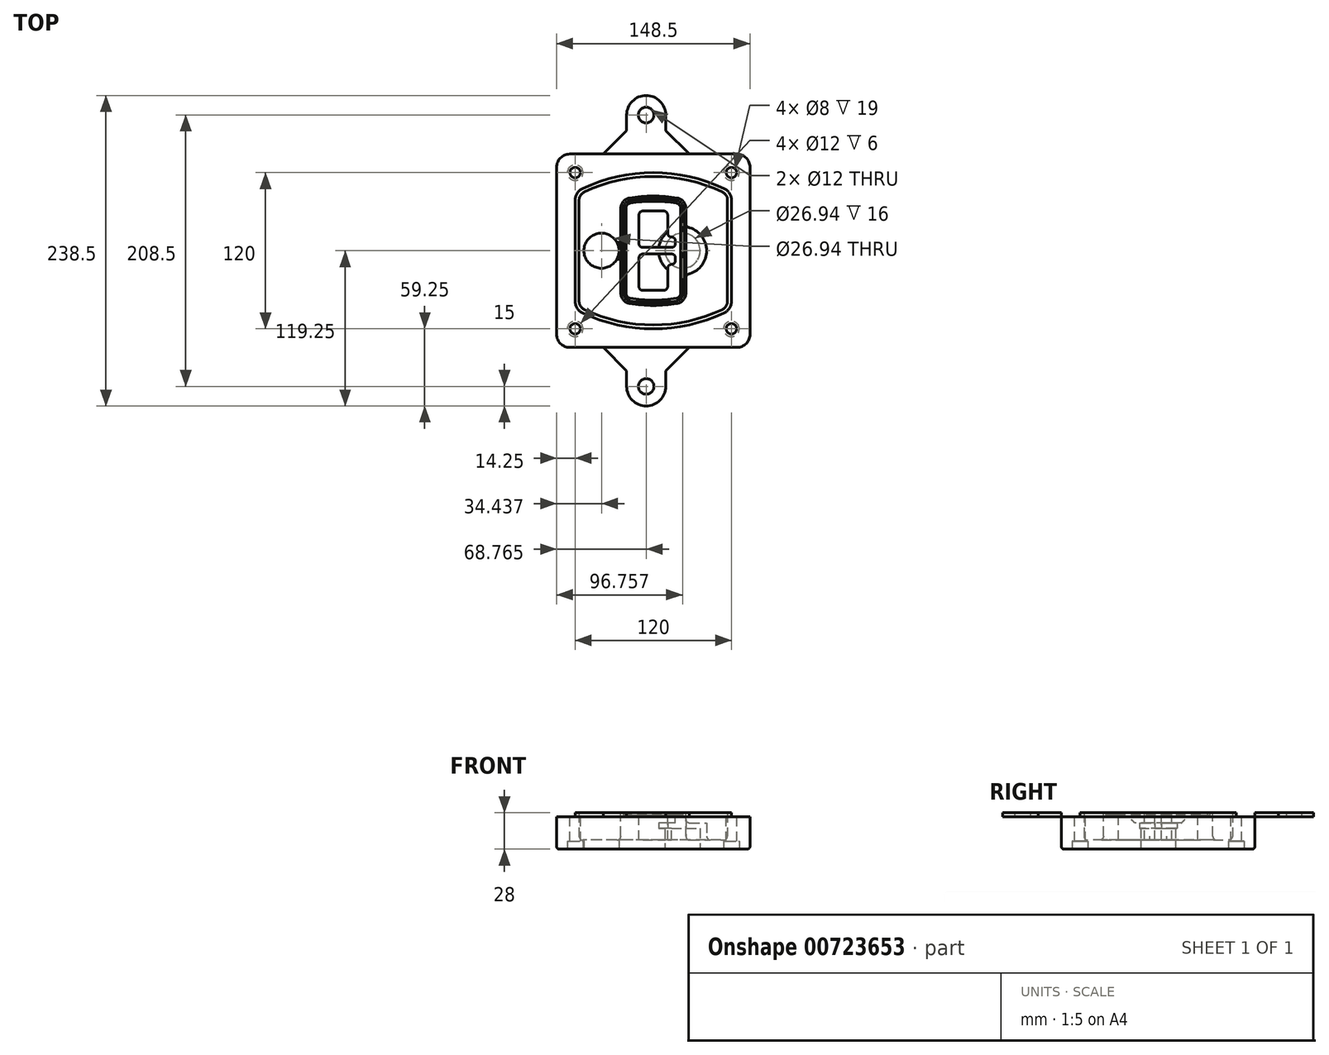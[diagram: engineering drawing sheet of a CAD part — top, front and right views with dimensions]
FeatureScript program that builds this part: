
annotation { "Feature Type Name" : "Feature", "Feature Type Description" : "" }
export const myFeature = defineFeature(function(context is Context, id is Id, definition is map)
    precondition{}
    {
        {
            var Q0;
            Q0=qCreatedBy(makeId("Top.planeOp"),FACE);
            var sketch = newSketch(context, id + "F0", { "sketchPlane" : qUnion([Q0])});
            skPoint(sketch, "E0.rect.middle", {"position": v(0, 0) * mm});
            skLineSegment(sketch, "E1.bottom", {"start": v(-64.25, -74.25) * mm, "end": v(64.25, -74.25) * mm});
            skLineSegment(sketch, "E1.top", {"start": v(-64.25, 74.25) * mm, "end": v(64.25, 74.25) * mm});
            skLineSegment(sketch, "E1.left", {"start": v(-74.25, -64.25) * mm, "end": v(-74.25, 64.25) * mm});
            skLineSegment(sketch, "E1.right", {"start": v(74.25, -64.25) * mm, "end": v(74.25, 64.25) * mm});
            skLineSegment(sketch, "E2", {"start": v(-74.25, 74.25) * mm, "end": v(74.25, -74.25) * mm, "construction": true});
            skLineSegment(sketch, "E3", {"start": v(74.25, 74.25) * mm, "end": v(-74.25, -74.25) * mm, "construction": true});
            skCircle(sketch, "E4", {"center": v(-60, 60) * mm, "radius": 4 * mm});
            skCircle(sketch, "E5", {"center": v(60, 60) * mm, "radius": 4 * mm});
            skCircle(sketch, "E6", {"center": v(60, -60) * mm, "radius": 4 * mm});
            skCircle(sketch, "E7", {"center": v(-60, -60) * mm, "radius": 4 * mm});
            skLineSegment(sketch, "E8", {"start": v(-60, 60) * mm, "end": v(60, 60) * mm, "construction": true});
            skLineSegment(sketch, "E9", {"start": v(60, 60) * mm, "end": v(60, -60) * mm, "construction": true});
            skLineSegment(sketch, "E10", {"start": v(60, -60) * mm, "end": v(-60, -60) * mm, "construction": true});
            skLineSegment(sketch, "E11", {"start": v(-60, -60) * mm, "end": v(-60, 60) * mm, "construction": true});
            skLineSegment(sketch, "E12", {"start": v(-60, 38.83) * mm, "end": v(-60, -38.83) * mm});
            skLineSegment(sketch, "E13", {"start": v(60, 38.83) * mm, "end": v(60, -38.83) * mm});
            skArc(sketch, "E14", {"start": v(54.26, 47.88) * mm, "mid": v(0, 60) * mm, "end": v(-54.26, 47.88) * mm});
            skArc(sketch, "E15", {"start": v(-54.26, -47.88) * mm, "mid": v(0, -60) * mm, "end": v(54.26, -47.88) * mm});
            skLineSegment(sketch, "E16", {"start": v(-60, 0) * mm, "end": v(60, 0) * mm, "construction": true});
            skPoint(sketch, "E17.visualSharp", {"position": v(-60, -45) * mm});
            skArc(sketch, "E17.filletArc", {"start": v(-60, -38.83) * mm, "mid": v(-58.44, -44.2) * mm, "end": v(-54.26, -47.88) * mm});
            skPoint(sketch, "E18.visualSharp", {"position": v(-60, 45) * mm});
            skArc(sketch, "E18.filletArc", {"start": v(-54.26, 47.88) * mm, "mid": v(-58.44, 44.2) * mm, "end": v(-60, 38.83) * mm});
            skPoint(sketch, "E19.visualSharp", {"position": v(60, 45) * mm});
            skArc(sketch, "E19.filletArc", {"start": v(60, 38.83) * mm, "mid": v(58.44, 44.2) * mm, "end": v(54.26, 47.88) * mm});
            skPoint(sketch, "E20.visualSharp", {"position": v(60, -45) * mm});
            skArc(sketch, "E20.filletArc", {"start": v(54.26, -47.88) * mm, "mid": v(58.44, -44.2) * mm, "end": v(60, -38.83) * mm});
            skPoint(sketch, "E21.visualSharp", {"position": v(-74.25, 74.25) * mm});
            skArc(sketch, "E21.filletArc", {"start": v(-64.25, 74.25) * mm, "mid": v(-71.32, 71.32) * mm, "end": v(-74.25, 64.25) * mm});
            skPoint(sketch, "E22.visualSharp", {"position": v(74.25, 74.25) * mm});
            skArc(sketch, "E22.filletArc", {"start": v(74.25, 64.25) * mm, "mid": v(71.32, 71.32) * mm, "end": v(64.25, 74.25) * mm});
            skPoint(sketch, "E23.visualSharp", {"position": v(74.25, -74.25) * mm});
            skArc(sketch, "E23.filletArc", {"start": v(64.25, -74.25) * mm, "mid": v(71.32, -71.32) * mm, "end": v(74.25, -64.25) * mm});
            skPoint(sketch, "E24.visualSharp", {"position": v(-74.25, -74.25) * mm});
            skArc(sketch, "E24.filletArc", {"start": v(-74.25, -64.25) * mm, "mid": v(-71.32, -71.32) * mm, "end": v(-64.25, -74.25) * mm});
            skArc(sketch, "E25.0", {"start": v(57, 38.83) * mm, "mid": v(55.9, 42.58) * mm, "end": v(52.98, 45.17) * mm});
            skLineSegment(sketch, "E25.1", {"start": v(57, 38.83) * mm, "end": v(57, -38.83) * mm});
            skArc(sketch, "E25.2", {"start": v(52.98, -45.17) * mm, "mid": v(55.9, -42.58) * mm, "end": v(57, -38.83) * mm});
            skArc(sketch, "E25.3", {"start": v(-52.98, -45.17) * mm, "mid": v(0, -57) * mm, "end": v(52.98, -45.17) * mm});
            skArc(sketch, "E25.4", {"start": v(-57, -38.83) * mm, "mid": v(-55.9, -42.58) * mm, "end": v(-52.98, -45.17) * mm});
            skArc(sketch, "E25.5", {"start": v(52.98, 45.17) * mm, "mid": v(0, 57) * mm, "end": v(-52.98, 45.17) * mm});
            skLineSegment(sketch, "E25.6", {"start": v(-57, 38.83) * mm, "end": v(-57, -38.83) * mm});
            skArc(sketch, "E25.7", {"start": v(-52.98, 45.17) * mm, "mid": v(-55.9, 42.58) * mm, "end": v(-57, 38.83) * mm});
            skArc(sketch, "E26.0", {"start": v(-55.96, 51.5) * mm, "mid": v(-61.82, 46.33) * mm, "end": v(-64, 38.83) * mm});
            skArc(sketch, "E26.1", {"start": v(55.96, 51.5) * mm, "mid": v(0, 64) * mm, "end": v(-55.96, 51.5) * mm});
            skArc(sketch, "E26.2", {"start": v(64, 38.83) * mm, "mid": v(61.82, 46.33) * mm, "end": v(55.96, 51.5) * mm});
            skLineSegment(sketch, "E26.3", {"start": v(64, 38.83) * mm, "end": v(64, -38.83) * mm});
            skArc(sketch, "E26.4", {"start": v(55.96, -51.5) * mm, "mid": v(61.82, -46.33) * mm, "end": v(64, -38.83) * mm});
            skLineSegment(sketch, "E26.5", {"start": v(-64, 38.83) * mm, "end": v(-64, -38.83) * mm});
            skArc(sketch, "E26.6", {"start": v(-55.96, -51.5) * mm, "mid": v(0, -64) * mm, "end": v(55.96, -51.5) * mm});
            skArc(sketch, "E26.7", {"start": v(-64, -38.83) * mm, "mid": v(-61.82, -46.33) * mm, "end": v(-55.96, -51.5) * mm});
            skSolve(sketch);
        }
        {
            var Q0;
            Q0=makeQuery(id+"F0.imprint","IMPRINT",FACE,{"disambiguationData":[TD([[makeQuery(id+"F0.imprint","IMPRINT",EDGE,{"derivedFrom":sQuery(id+"F0.wireOp",EDGE,"E1.bottom")}),1.0]])]});
            var Q1;
            Q1=makeQuery(id+"F0.imprint","IMPRINT",FACE,{"disambiguationData":[TD([[makeQuery(id+"F0.imprint","IMPRINT",EDGE,{"derivedFrom":sQuery(id+"F0.wireOp",EDGE,"E12")}),1.0]])]});
            var Q2;
            Q2=makeQuery(id+"F0.imprint","IMPRINT",FACE,{"disambiguationData":[TD([[makeQuery(id+"F0.imprint","IMPRINT",EDGE,{"derivedFrom":sQuery(id+"F0.wireOp",EDGE,"E25.0")}),1.0]])]});
            var Q3;
            Q3=makeQuery(id+"F0.imprint","IMPRINT",FACE,{"disambiguationData":[TD([[makeQuery(id+"F0.imprint","IMPRINT",EDGE,{"derivedFrom":sQuery(id+"F0.wireOp",EDGE,"E12")}),-1.0]])]});
            extrude(context, id + "F1", {"entities" : qUnion([Q0, Q1, Q2, Q3]), "oppositeDirection" : true, "depth" : 25 * mm});
        }
        {
            var Q0;
            Q0=makeQuery(id+"F0.imprint","IMPRINT",FACE,{"disambiguationData":[TD([[makeQuery(id+"F0.imprint","IMPRINT",EDGE,{"derivedFrom":sQuery(id+"F0.wireOp",EDGE,"E12")}),1.0]])]});
            extrude(context, id + "F2", {"entities" : qUnion([Q0]), "operationType" : NewBodyOperationType.ADD, "depth" : 3 * mm, "offsetDistance" : 25 * mm});
        }
        {
            var Q0;
            Q0=makeQuery(id+"F0.imprint","IMPRINT",FACE,{"disambiguationData":[TD([[makeQuery(id+"F0.imprint","IMPRINT",EDGE,{"derivedFrom":sQuery(id+"F0.wireOp",EDGE,"E25.0")}),1.0]])]});
            extrude(context, id + "F3", {"entities" : qUnion([Q0]), "operationType" : NewBodyOperationType.REMOVE, "oppositeDirection" : true, "depth" : 18 * mm});
        }
        {
            var Q0;
            Q0=makeQuery(id+"F2.opExtrude","CAP_FACE",FACE,{"disambiguationData":[OSD([sQuery(id+"F0.wireOp",EDGE,"E12"),sQuery(id+"F0.wireOp",EDGE,"E13"),sQuery(id+"F0.wireOp",EDGE,"E14"),sQuery(id+"F0.wireOp",EDGE,"E15"),sQuery(id+"F0.wireOp",EDGE,"E17.filletArc"),sQuery(id+"F0.wireOp",EDGE,"E18.filletArc"),sQuery(id+"F0.wireOp",EDGE,"E19.filletArc"),sQuery(id+"F0.wireOp",EDGE,"E20.filletArc"),sQuery(id+"F0.wireOp",EDGE,"E25.0"),sQuery(id+"F0.wireOp",EDGE,"E25.1"),sQuery(id+"F0.wireOp",EDGE,"E25.2"),sQuery(id+"F0.wireOp",EDGE,"E25.3"),sQuery(id+"F0.wireOp",EDGE,"E25.4"),sQuery(id+"F0.wireOp",EDGE,"E25.5"),sQuery(id+"F0.wireOp",EDGE,"E25.6"),sQuery(id+"F0.wireOp",EDGE,"E25.7")])],"isStart":false});
            var sketch = newSketch(context, id + "F4", { "sketchPlane" : qUnion([Q0])});
            skArc(sketch, "E27.0", {"start": v(-18.34, -40.45) * mm, "mid": v(0, -42) * mm, "end": v(18.34, -40.45) * mm});
            skArc(sketch, "E28.0", {"start": v(18.34, 40.45) * mm, "mid": v(0, 42) * mm, "end": v(-18.34, 40.45) * mm});
            skLineSegment(sketch, "E29", {"start": v(-25, 32.57) * mm, "end": v(-25, -32.57) * mm});
            skLineSegment(sketch, "E30", {"start": v(25, 32.57) * mm, "end": v(25, -32.57) * mm});
            skLineSegment(sketch, "E31", {"start": v(-25, 39.1) * mm, "end": v(25, 39.1) * mm, "construction": true});
            skLineSegment(sketch, "E32", {"start": v(-25, -39.1) * mm, "end": v(25, -39.1) * mm, "construction": true});
            skPoint(sketch, "E33.visualSharp", {"position": v(-25, 39.1) * mm});
            skArc(sketch, "E33.filletArc", {"start": v(-18.34, 40.45) * mm, "mid": v(-23.11, 37.73) * mm, "end": v(-25, 32.57) * mm});
            skPoint(sketch, "E34.visualSharp", {"position": v(25, 39.1) * mm});
            skArc(sketch, "E34.filletArc", {"start": v(25, 32.57) * mm, "mid": v(23.11, 37.73) * mm, "end": v(18.34, 40.45) * mm});
            skPoint(sketch, "E35.visualSharp", {"position": v(25, -39.1) * mm});
            skArc(sketch, "E35.filletArc", {"start": v(18.34, -40.45) * mm, "mid": v(23.11, -37.73) * mm, "end": v(25, -32.57) * mm});
            skPoint(sketch, "E36.visualSharp", {"position": v(-25, -39.1) * mm});
            skArc(sketch, "E36.filletArc", {"start": v(-25, -32.57) * mm, "mid": v(-23.11, -37.73) * mm, "end": v(-18.34, -40.45) * mm});
            skArc(sketch, "E37.0", {"start": v(52.98, 45.17) * mm, "mid": v(0, 57) * mm, "end": v(-52.98, 45.17) * mm});
            skArc(sketch, "E37.1", {"start": v(-52.98, 45.17) * mm, "mid": v(-55.9, 42.58) * mm, "end": v(-57, 38.83) * mm});
            skLineSegment(sketch, "E37.2", {"start": v(-57, 38.83) * mm, "end": v(-57, -38.83) * mm});
            skArc(sketch, "E37.3", {"start": v(-57, -38.83) * mm, "mid": v(-55.9, -42.58) * mm, "end": v(-52.98, -45.17) * mm});
            skArc(sketch, "E37.4", {"start": v(-52.98, -45.17) * mm, "mid": v(0, -57) * mm, "end": v(52.98, -45.17) * mm});
            skArc(sketch, "E37.5", {"start": v(52.98, -45.17) * mm, "mid": v(55.9, -42.58) * mm, "end": v(57, -38.83) * mm});
            skLineSegment(sketch, "E37.6", {"start": v(57, 38.83) * mm, "end": v(57, -38.83) * mm});
            skArc(sketch, "E37.7", {"start": v(57, 38.83) * mm, "mid": v(55.9, 42.58) * mm, "end": v(52.98, 45.17) * mm});
            skLineSegment(sketch, "E38.0", {"start": v(23, 32.57) * mm, "end": v(23, -32.57) * mm});
            skArc(sketch, "E38.1", {"start": v(18, -38.48) * mm, "mid": v(21.58, -36.44) * mm, "end": v(23, -32.57) * mm});
            skArc(sketch, "E38.2", {"start": v(-18, -38.48) * mm, "mid": v(0, -40) * mm, "end": v(18, -38.48) * mm});
            skArc(sketch, "E38.3", {"start": v(-23, -32.57) * mm, "mid": v(-21.58, -36.44) * mm, "end": v(-18, -38.48) * mm});
            skLineSegment(sketch, "E38.4", {"start": v(-23, 32.57) * mm, "end": v(-23, -32.57) * mm});
            skArc(sketch, "E38.5", {"start": v(23, 32.57) * mm, "mid": v(21.58, 36.44) * mm, "end": v(18, 38.48) * mm});
            skArc(sketch, "E38.6", {"start": v(-18, 38.48) * mm, "mid": v(-21.58, 36.44) * mm, "end": v(-23, 32.57) * mm});
            skArc(sketch, "E38.7", {"start": v(18, 38.48) * mm, "mid": v(0, 40) * mm, "end": v(-18, 38.48) * mm});
            skArc(sketch, "E39.0", {"start": v(21, 32.57) * mm, "mid": v(20.06, 35.15) * mm, "end": v(17.67, 36.5) * mm});
            skLineSegment(sketch, "E39.1", {"start": v(21, 32.57) * mm, "end": v(21, -32.57) * mm});
            skArc(sketch, "E39.2", {"start": v(17.67, -36.5) * mm, "mid": v(20.06, -35.15) * mm, "end": v(21, -32.57) * mm});
            skArc(sketch, "E39.3", {"start": v(-17.67, -36.5) * mm, "mid": v(0, -38) * mm, "end": v(17.67, -36.5) * mm});
            skArc(sketch, "E39.4", {"start": v(-21, -32.57) * mm, "mid": v(-20.06, -35.15) * mm, "end": v(-17.67, -36.5) * mm});
            skArc(sketch, "E39.5", {"start": v(17.67, 36.5) * mm, "mid": v(0, 38) * mm, "end": v(-17.67, 36.5) * mm});
            skLineSegment(sketch, "E39.6", {"start": v(-21, 32.57) * mm, "end": v(-21, -32.57) * mm});
            skArc(sketch, "E39.7", {"start": v(-17.67, 36.5) * mm, "mid": v(-20.06, 35.15) * mm, "end": v(-21, 32.57) * mm});
            skLineSegment(sketch, "E40", {"start": v(-25, 0) * mm, "end": v(25, 0) * mm, "construction": true});
            skLineSegment(sketch, "E41", {"start": v(-11, 5.5) * mm, "end": v(-11, 27.5) * mm});
            skLineSegment(sketch, "E42", {"start": v(-8, 30.5) * mm, "end": v(8, 30.5) * mm});
            skLineSegment(sketch, "E43", {"start": v(11, 27.5) * mm, "end": v(11, 13.5) * mm});
            skLineSegment(sketch, "E44", {"start": v(14, 10.5) * mm, "end": v(14, 10.5) * mm});
            skLineSegment(sketch, "E45", {"start": v(17, 7.5) * mm, "end": v(17, 5.5) * mm});
            skLineSegment(sketch, "E46", {"start": v(14, 2.5) * mm, "end": v(-8, 2.5) * mm});
            skPoint(sketch, "E47.visualSharp", {"position": v(-11, 30.5) * mm});
            skArc(sketch, "E47.filletArc", {"start": v(-8, 30.5) * mm, "mid": v(-10.12, 29.62) * mm, "end": v(-11, 27.5) * mm});
            skPoint(sketch, "E48.visualSharp", {"position": v(11, 30.5) * mm});
            skArc(sketch, "E48.filletArc", {"start": v(11, 27.5) * mm, "mid": v(10.12, 29.62) * mm, "end": v(8, 30.5) * mm});
            skPoint(sketch, "E49.visualSharp", {"position": v(11, 10.5) * mm});
            skArc(sketch, "E49.filletArc", {"start": v(11, 13.5) * mm, "mid": v(11.88, 11.38) * mm, "end": v(14, 10.5) * mm});
            skPoint(sketch, "E50.visualSharp", {"position": v(17, 10.5) * mm});
            skArc(sketch, "E50.filletArc", {"start": v(17, 7.5) * mm, "mid": v(16.12, 9.62) * mm, "end": v(14, 10.5) * mm});
            skPoint(sketch, "E51.visualSharp", {"position": v(17, 2.5) * mm});
            skArc(sketch, "E51.filletArc", {"start": v(14, 2.5) * mm, "mid": v(16.12, 3.38) * mm, "end": v(17, 5.5) * mm});
            skPoint(sketch, "E52.visualSharp", {"position": v(-11, 2.5) * mm});
            skArc(sketch, "E52.filletArc", {"start": v(-11, 5.5) * mm, "mid": v(-10.12, 3.38) * mm, "end": v(-8, 2.5) * mm});
            skLineSegment(sketch, "E53.0.MirrorCS", {"start": v(14, -2.5) * mm, "end": v(-8, -2.5) * mm});
            skArc(sketch, "E54.0.MirrorCS", {"start": v(-11, -5.5) * mm, "mid": v(-10.12, -3.38) * mm, "end": v(-8, -2.5) * mm});
            skLineSegment(sketch, "E55.0.MirrorCS", {"start": v(-11, -5.5) * mm, "end": v(-11, -27.5) * mm});
            skArc(sketch, "E56.0.MirrorCS", {"start": v(-8, -30.5) * mm, "mid": v(-10.12, -29.62) * mm, "end": v(-11, -27.5) * mm});
            skLineSegment(sketch, "E57.0.MirrorCS", {"start": v(-8, -30.5) * mm, "end": v(8, -30.5) * mm});
            skArc(sketch, "E58.0.MirrorCS", {"start": v(11, -27.5) * mm, "mid": v(10.12, -29.62) * mm, "end": v(8, -30.5) * mm});
            skLineSegment(sketch, "E59.0.MirrorCS", {"start": v(11, -27.5) * mm, "end": v(11, -13.5) * mm});
            skArc(sketch, "E60.0.MirrorCS", {"start": v(11, -13.5) * mm, "mid": v(11.88, -11.38) * mm, "end": v(14, -10.5) * mm});
            skArc(sketch, "E61.0.MirrorCS", {"start": v(17, -7.5) * mm, "mid": v(16.12, -9.62) * mm, "end": v(14, -10.5) * mm});
            skLineSegment(sketch, "E62.0.MirrorCS", {"start": v(17, -7.5) * mm, "end": v(17, -5.5) * mm});
            skArc(sketch, "E63.0.MirrorCS", {"start": v(14, -2.5) * mm, "mid": v(16.12, -3.38) * mm, "end": v(17, -5.5) * mm});
            skSolve(sketch);
        }
        {
            var Q0;
            Q0=makeQuery(id+"F4.imprint","IMPRINT",FACE,{"disambiguationData":[TD([[makeQuery(id+"F4.imprint","IMPRINT",EDGE,{"derivedFrom":sQuery(id+"F4.wireOp",EDGE,"E27.0")}),1.0]])]});
            var Q1;
            Q1=makeQuery(id+"F4.imprint","IMPRINT",FACE,{"disambiguationData":[TD([[makeQuery(id+"F4.imprint","IMPRINT",EDGE,{"derivedFrom":sQuery(id+"F4.wireOp",EDGE,"E38.0")}),-1.0]])]});
            var Q2;
            Q2=makeQuery(id+"F4.imprint","IMPRINT",FACE,{"disambiguationData":[TD([[makeQuery(id+"F4.imprint","IMPRINT",EDGE,{"derivedFrom":sQuery(id+"F4.wireOp",EDGE,"E39.0")}),1.0]])]});
            extrude(context, id + "F5", {"entities" : qUnion([Q0, Q1, Q2]), "operationType" : NewBodyOperationType.ADD, "endBound" : BoundingType.UP_TO_NEXT, "oppositeDirection" : true, "depth" : 25 * mm});
        }
        {
            var Q0;
            Q0=makeQuery(id+"F4.imprint","IMPRINT",FACE,{"disambiguationData":[TD([[makeQuery(id+"F4.imprint","IMPRINT",EDGE,{"derivedFrom":sQuery(id+"F4.wireOp",EDGE,"E38.0")}),-1.0]])]});
            extrude(context, id + "F6", {"entities" : qUnion([Q0]), "operationType" : NewBodyOperationType.REMOVE, "oppositeDirection" : true, "depth" : 2 * mm});
        }
        {
            var Q0;
            Q0=makeQuery(id+"F1.opExtrude","CAP_FACE",FACE,{"disambiguationData":[OSD([sQuery(id+"F0.wireOp",EDGE,"E1.bottom"),sQuery(id+"F0.wireOp",EDGE,"E1.top"),sQuery(id+"F0.wireOp",EDGE,"E1.left"),sQuery(id+"F0.wireOp",EDGE,"E1.right"),sQuery(id+"F0.wireOp",EDGE,"E4"),sQuery(id+"F0.wireOp",EDGE,"E5"),sQuery(id+"F0.wireOp",EDGE,"E6"),sQuery(id+"F0.wireOp",EDGE,"E7"),sQuery(id+"F0.wireOp",EDGE,"E21.filletArc"),sQuery(id+"F0.wireOp",EDGE,"E22.filletArc"),sQuery(id+"F0.wireOp",EDGE,"E23.filletArc"),sQuery(id+"F0.wireOp",EDGE,"E24.filletArc")])],"isStart":false});
            var sketch = newSketch(context, id + "F7", { "sketchPlane" : qUnion([Q0])});
            skCircle(sketch, "E64", {"center": v(22.5, 0) * mm, "radius": 13.47 * mm});
            skCircle(sketch, "E65", {"center": v(-39.81, 0) * mm, "radius": 13.47 * mm});
            skLineSegment(sketch, "E66", {"start": v(74.25, 0) * mm, "end": v(-74.25, 0) * mm});
            skCircle(sketch, "E67", {"center": v(22.5, 0) * mm, "radius": 18.47 * mm});
            skCircle(sketch, "E68", {"center": v(60, -60) * mm, "radius": 6 * mm});
            skCircle(sketch, "E69", {"center": v(-60, -60) * mm, "radius": 6 * mm});
            skCircle(sketch, "E70", {"center": v(-60, 60) * mm, "radius": 6 * mm});
            skCircle(sketch, "E71", {"center": v(60, 60) * mm, "radius": 6 * mm});
            skSolve(sketch);
        }
        {
            var Q0;
            {var subQ1=sQuery(id+"F7.wireOp",EDGE,"E66");var subQ4=sQuery(id+"F7.wireOp",EDGE,"E64");var subQ6=makeQuery(id+"F7.imprint","INTERSECT",VERTEX,{"disambiguationData":[OD(0.0)],"derivedFrom":[subQ4,subQ1]});Q0=makeQuery(id+"F7.imprint","IMPRINT",FACE,{"disambiguationData":[TD([[makeQuery(id+"F7.imprint","IMPRINT",EDGE,{"disambiguationData":[TD([[subQ6,-1.0]])],"derivedFrom":subQ4}),-1.0]])]});}
            var Q1;
            {var subQ0=sQuery(id+"F7.wireOp",EDGE,"E66");var subQ1=sQuery(id+"F7.wireOp",EDGE,"E64");var subQ3=makeQuery(id+"F7.imprint","INTERSECT",VERTEX,{"disambiguationData":[OD(0.0)],"derivedFrom":[subQ1,subQ0]});Q1=makeQuery(id+"F7.imprint","IMPRINT",FACE,{"disambiguationData":[TD([[makeQuery(id+"F7.imprint","IMPRINT",EDGE,{"disambiguationData":[TD([[subQ3,-1.0]])],"derivedFrom":subQ1}),1.0]])]});}
            var Q2;
            {var subQ0=sQuery(id+"F7.wireOp",EDGE,"E66");var subQ1=sQuery(id+"F7.wireOp",EDGE,"E64");var subQ3=makeQuery(id+"F7.imprint","INTERSECT",VERTEX,{"disambiguationData":[OD(0.0)],"derivedFrom":[subQ1,subQ0]});Q2=makeQuery(id+"F7.imprint","IMPRINT",FACE,{"disambiguationData":[TD([[makeQuery(id+"F7.imprint","IMPRINT",EDGE,{"disambiguationData":[TD([[subQ3,1.0]])],"derivedFrom":subQ1}),1.0]])]});}
            var Q3;
            {var subQ1=sQuery(id+"F7.wireOp",EDGE,"E66");var subQ4=sQuery(id+"F7.wireOp",EDGE,"E64");var subQ6=makeQuery(id+"F7.imprint","INTERSECT",VERTEX,{"disambiguationData":[OD(0.0)],"derivedFrom":[subQ4,subQ1]});Q3=makeQuery(id+"F7.imprint","IMPRINT",FACE,{"disambiguationData":[TD([[makeQuery(id+"F7.imprint","IMPRINT",EDGE,{"disambiguationData":[TD([[subQ6,1.0]])],"derivedFrom":subQ4}),-1.0]])]});}
            extrude(context, id + "F8", {"entities" : qUnion([Q0, Q1, Q2, Q3]), "operationType" : NewBodyOperationType.ADD, "oppositeDirection" : true, "depth" : 20 * mm});
        }
        {
            var Q0;
            {var subQ0=sQuery(id+"F7.wireOp",EDGE,"E66");var subQ1=sQuery(id+"F7.wireOp",EDGE,"E64");var subQ3=makeQuery(id+"F7.imprint","INTERSECT",VERTEX,{"disambiguationData":[OD(0.0)],"derivedFrom":[subQ1,subQ0]});Q0=makeQuery(id+"F7.imprint","IMPRINT",FACE,{"disambiguationData":[TD([[makeQuery(id+"F7.imprint","IMPRINT",EDGE,{"disambiguationData":[TD([[subQ3,-1.0]])],"derivedFrom":subQ1}),1.0]])]});}
            var Q1;
            {var subQ0=sQuery(id+"F7.wireOp",EDGE,"E66");var subQ1=sQuery(id+"F7.wireOp",EDGE,"E64");var subQ3=makeQuery(id+"F7.imprint","INTERSECT",VERTEX,{"disambiguationData":[OD(0.0)],"derivedFrom":[subQ1,subQ0]});Q1=makeQuery(id+"F7.imprint","IMPRINT",FACE,{"disambiguationData":[TD([[makeQuery(id+"F7.imprint","IMPRINT",EDGE,{"disambiguationData":[TD([[subQ3,1.0]])],"derivedFrom":subQ1}),1.0]])]});}
            extrude(context, id + "F9", {"entities" : qUnion([Q0, Q1]), "operationType" : NewBodyOperationType.REMOVE, "oppositeDirection" : true, "depth" : 16 * mm});
        }
        {
            var Q0;
            {var subQ0=sQuery(id+"F7.wireOp",EDGE,"E66");var subQ1=sQuery(id+"F7.wireOp",EDGE,"E65");var subQ3=makeQuery(id+"F7.imprint","INTERSECT",VERTEX,{"disambiguationData":[OD(0.0)],"derivedFrom":[subQ1,subQ0]});Q0=makeQuery(id+"F7.imprint","IMPRINT",FACE,{"disambiguationData":[TD([[makeQuery(id+"F7.imprint","IMPRINT",EDGE,{"disambiguationData":[TD([[subQ3,-1.0]])],"derivedFrom":subQ1}),1.0]])]});}
            var Q1;
            {var subQ0=sQuery(id+"F7.wireOp",EDGE,"E66");var subQ1=sQuery(id+"F7.wireOp",EDGE,"E65");var subQ3=makeQuery(id+"F7.imprint","INTERSECT",VERTEX,{"disambiguationData":[OD(0.0)],"derivedFrom":[subQ1,subQ0]});Q1=makeQuery(id+"F7.imprint","IMPRINT",FACE,{"disambiguationData":[TD([[makeQuery(id+"F7.imprint","IMPRINT",EDGE,{"disambiguationData":[TD([[subQ3,1.0]])],"derivedFrom":subQ1}),1.0]])]});}
            extrude(context, id + "F10", {"entities" : qUnion([Q0, Q1]), "operationType" : NewBodyOperationType.REMOVE, "oppositeDirection" : true, "depth" : 25 * mm});
        }
        {
            var Q0;
            Q0=makeQuery(id+"F7.imprint","IMPRINT",FACE,{"disambiguationData":[TD([[makeQuery(id+"F7.imprint","IMPRINT",EDGE,{"derivedFrom":sQuery(id+"F7.wireOp",EDGE,"E68")}),1.0]])]});
            var Q1;
            Q1=makeQuery(id+"F7.imprint","IMPRINT",FACE,{"disambiguationData":[TD([[makeQuery(id+"F7.imprint","IMPRINT",EDGE,{"derivedFrom":makeQuery(id+"F1.opExtrude","CAP_EDGE",EDGE,{"disambiguationData":[OSD([sQuery(id+"F0.wireOp",EDGE,"E5")])],"isStart":false})}),-1.0]])]});
            var Q2;
            Q2=makeQuery(id+"F7.imprint","IMPRINT",FACE,{"disambiguationData":[TD([[makeQuery(id+"F7.imprint","IMPRINT",EDGE,{"derivedFrom":sQuery(id+"F7.wireOp",EDGE,"E69")}),1.0]])]});
            var Q3;
            Q3=makeQuery(id+"F7.imprint","IMPRINT",FACE,{"disambiguationData":[TD([[makeQuery(id+"F7.imprint","IMPRINT",EDGE,{"derivedFrom":makeQuery(id+"F1.opExtrude","CAP_EDGE",EDGE,{"disambiguationData":[OSD([sQuery(id+"F0.wireOp",EDGE,"E4")])],"isStart":false})}),-1.0]])]});
            var Q4;
            Q4=makeQuery(id+"F7.imprint","IMPRINT",FACE,{"disambiguationData":[TD([[makeQuery(id+"F7.imprint","IMPRINT",EDGE,{"derivedFrom":sQuery(id+"F7.wireOp",EDGE,"E70")}),1.0]])]});
            var Q5;
            Q5=makeQuery(id+"F7.imprint","IMPRINT",FACE,{"disambiguationData":[TD([[makeQuery(id+"F7.imprint","IMPRINT",EDGE,{"derivedFrom":makeQuery(id+"F1.opExtrude","CAP_EDGE",EDGE,{"disambiguationData":[OSD([sQuery(id+"F0.wireOp",EDGE,"E7")])],"isStart":false})}),-1.0]])]});
            var Q6;
            Q6=makeQuery(id+"F7.imprint","IMPRINT",FACE,{"disambiguationData":[TD([[makeQuery(id+"F7.imprint","IMPRINT",EDGE,{"derivedFrom":sQuery(id+"F7.wireOp",EDGE,"E71")}),1.0]])]});
            var Q7;
            Q7=makeQuery(id+"F7.imprint","IMPRINT",FACE,{"disambiguationData":[TD([[makeQuery(id+"F7.imprint","IMPRINT",EDGE,{"derivedFrom":makeQuery(id+"F1.opExtrude","CAP_EDGE",EDGE,{"disambiguationData":[OSD([sQuery(id+"F0.wireOp",EDGE,"E6")])],"isStart":false})}),-1.0]])]});
            extrude(context, id + "F11", {"entities" : qUnion([Q0, Q1, Q2, Q3, Q4, Q5, Q6, Q7]), "operationType" : NewBodyOperationType.REMOVE, "oppositeDirection" : true, "depth" : 6 * mm});
        }
        {
            var Q0;
            Q0=makeQuery(id+"F9.boolean.opBoolean","COPY",FACE,{"derivedFrom":makeQuery(id+"F9.opExtrude","CAP_FACE",FACE,{"disambiguationData":[OSD([sQuery(id+"F7.wireOp",EDGE,"E64")])],"isStart":false})});
            var sketch = newSketch(context, id + "F12", { "sketchPlane" : qUnion([Q0])});
            skArc(sketch, "E72.0", {"start": v(11, 14.45) * mm, "mid": v(6.45, 9.13) * mm, "end": v(4.2, 2.5) * mm});
            skArc(sketch, "E72.1", {"start": v(4.2, -2.5) * mm, "mid": v(6.45, -9.13) * mm, "end": v(11, -14.45) * mm});
            skLineSegment(sketch, "E73", {"start": v(4.2, -2.5) * mm, "end": v(14, -2.5) * mm});
            skLineSegment(sketch, "E74.0", {"start": v(14, 2.5) * mm, "end": v(4.2, 2.5) * mm});
            skArc(sketch, "E74.1", {"start": v(14, 2.5) * mm, "mid": v(16.12, 3.38) * mm, "end": v(17, 5.5) * mm});
            skLineSegment(sketch, "E74.2", {"start": v(17, 7.5) * mm, "end": v(17, 5.5) * mm});
            skArc(sketch, "E74.3", {"start": v(17, 7.5) * mm, "mid": v(16.12, 9.62) * mm, "end": v(14, 10.5) * mm});
            skArc(sketch, "E74.4", {"start": v(11, 13.5) * mm, "mid": v(11.88, 11.38) * mm, "end": v(14, 10.5) * mm});
            skLineSegment(sketch, "E74.5", {"start": v(11, 14.45) * mm, "end": v(11, 13.5) * mm});
            skLineSegment(sketch, "E74.7", {"start": v(14, -2.5) * mm, "end": v(4.2, -2.5) * mm});
            skArc(sketch, "E74.8", {"start": v(14, -2.5) * mm, "mid": v(16.12, -3.38) * mm, "end": v(17, -5.5) * mm});
            skLineSegment(sketch, "E74.9", {"start": v(17, -7.5) * mm, "end": v(17, -5.5) * mm});
            skArc(sketch, "E74.10", {"start": v(17, -7.5) * mm, "mid": v(16.12, -9.62) * mm, "end": v(14, -10.5) * mm});
            skArc(sketch, "E74.11", {"start": v(11, -13.5) * mm, "mid": v(11.88, -11.38) * mm, "end": v(14, -10.5) * mm});
            skLineSegment(sketch, "E74.12", {"start": v(11, -14.45) * mm, "end": v(11, -13.5) * mm});
            skPoint(sketch, "E75.orphan", {"position": v(11, -27.5) * mm});
            skPoint(sketch, "E76.orphan", {"position": v(-8, -2.5) * mm});
            skPoint(sketch, "E77.orphan", {"position": v(-8, 2.5) * mm});
            skPoint(sketch, "E78.orphan", {"position": v(11, 27.5) * mm});
            skSolve(sketch);
        }
        {
            var Q0;
            {var subQ7=sQuery(id+"F12.wireOp",EDGE,"E72.0");var subQ14=sQuery(id+"F12.wireOp",EDGE,"E72.1");var subQ16=sQuery(id+"F12.wireOp",EDGE,"E74.1");var subQ18=sQuery(id+"F12.wireOp",EDGE,"E74.8");Q0=qUnion([makeQuery(id+"F12.imprint","IMPRINT",FACE,{"disambiguationData":[TD([[makeQuery(id+"F12.imprint","IMPRINT",EDGE,{"derivedFrom":subQ7}),1.0]])]}),makeQuery(id+"F12.imprint","IMPRINT",FACE,{"disambiguationData":[TD([[makeQuery(id+"F12.imprint","IMPRINT",EDGE,{"derivedFrom":subQ14}),1.0]])]}),makeQuery(id+"F12.imprint","IMPRINT",FACE,{"disambiguationData":[TD([[makeQuery(id+"F12.imprint","IMPRINT",EDGE,{"derivedFrom":subQ16}),1.0]])]}),makeQuery(id+"F12.imprint","IMPRINT",FACE,{"disambiguationData":[TD([[makeQuery(id+"F12.imprint","IMPRINT",EDGE,{"derivedFrom":subQ18}),-1.0]])]})]);}
            var Q1;
            Q1=makeQuery(id+"F5.boolean.opBoolean","SPLIT",FACE,{"disambiguationData":[TD([makeQuery(id+"F5.opExtrude","SWEPT_FACE",FACE,{"disambiguationData":[OSD([sQuery(id+"F4.wireOp",EDGE,"E41")])]})])],"derivedFrom":makeQuery(id+"F3.boolean.opBoolean","COPY",FACE,{"derivedFrom":makeQuery(id+"F3.opExtrude","CAP_FACE",FACE,{"disambiguationData":[OSD([sQuery(id+"F0.wireOp",EDGE,"E25.0"),sQuery(id+"F0.wireOp",EDGE,"E25.1"),sQuery(id+"F0.wireOp",EDGE,"E25.2"),sQuery(id+"F0.wireOp",EDGE,"E25.3"),sQuery(id+"F0.wireOp",EDGE,"E25.4"),sQuery(id+"F0.wireOp",EDGE,"E25.5"),sQuery(id+"F0.wireOp",EDGE,"E25.6"),sQuery(id+"F0.wireOp",EDGE,"E25.7")])],"isStart":false})})});
            extrude(context, id + "F13", {"entities" : qUnion([Q0]), "operationType" : NewBodyOperationType.REMOVE, "endBound" : BoundingType.UP_TO_SURFACE, "endBoundEntityFace" : qUnion([Q1]), "depth" : 25 * mm});
        }
        {
            var Q0;
            Q0=makeQuery(id+"F3.boolean.opBoolean","COPY",EDGE,{"derivedFrom":makeQuery(id+"F3.opExtrude","CAP_EDGE",EDGE,{"disambiguationData":[OSD([sQuery(id+"F0.wireOp",EDGE,"E25.6")])],"isStart":false})});
            var Q1;
            Q1=makeQuery(id+"F8.boolean.opBoolean","INTERSECT",EDGE,{"derivedFrom":[makeQuery(id+"F5.opExtrude","SWEPT_FACE",FACE,{"disambiguationData":[OSD([sQuery(id+"F4.wireOp",EDGE,"E30")])]}),makeQuery(id+"F8.opExtrude","CAP_FACE",FACE,{"disambiguationData":[OSD([sQuery(id+"F7.wireOp",EDGE,"E67")])],"isStart":false})]});
            var Q2;
            Q2=makeQuery(id+"F8.boolean.opBoolean","INTERSECT",EDGE,{"disambiguationData":[OD(1.0)],"derivedFrom":[makeQuery(id+"F5.opExtrude","SWEPT_FACE",FACE,{"disambiguationData":[OSD([sQuery(id+"F4.wireOp",EDGE,"E30")])]}),makeQuery(id+"F8.opExtrude","SWEPT_FACE",FACE,{"disambiguationData":[OSD([sQuery(id+"F7.wireOp",EDGE,"E67")])]})]});
            var Q3;
            {var subQ0=sQuery(id+"F4.wireOp",EDGE,"E30");Q3=makeQuery(id+"F8.boolean.opBoolean","SPLIT",EDGE,{"disambiguationData":[TD([makeQuery(id+"F5.opExtrude","SWEPT_FACE",FACE,{"disambiguationData":[OSD([sQuery(id+"F4.wireOp",EDGE,"E35.filletArc")])]})])],"derivedFrom":makeQuery(id+"F5.opExtrude","CAP_EDGE",EDGE,{"disambiguationData":[OSD([subQ0])],"isStart":false})});}
            var Q4;
            {var subQ0=sQuery(id+"F0.wireOp",EDGE,"E25.7");var subQ1=sQuery(id+"F0.wireOp",EDGE,"E25.1");var subQ2=sQuery(id+"F0.wireOp",EDGE,"E25.6");var subQ3=sQuery(id+"F0.wireOp",EDGE,"E25.5");var subQ4=sQuery(id+"F0.wireOp",EDGE,"E25.4");var subQ5=sQuery(id+"F0.wireOp",EDGE,"E25.0");var subQ6=sQuery(id+"F0.wireOp",EDGE,"E25.2");var subQ7=sQuery(id+"F0.wireOp",EDGE,"E25.3");Q4=makeQuery(id+"F8.boolean.opBoolean","INTERSECT",EDGE,{"derivedFrom":[makeQuery(id+"F5.boolean.opBoolean","SPLIT",FACE,{"disambiguationData":[TD([makeQuery(id+"F2.opExtrude","SWEPT_FACE",FACE,{"disambiguationData":[OSD([subQ5])]})])],"derivedFrom":makeQuery(id+"F3.boolean.opBoolean","COPY",FACE,{"derivedFrom":makeQuery(id+"F3.opExtrude","CAP_FACE",FACE,{"disambiguationData":[OSD([subQ5,subQ1,subQ6,subQ7,subQ4,subQ3,subQ2,subQ0])],"isStart":false})})}),makeQuery(id+"F8.opExtrude","SWEPT_FACE",FACE,{"disambiguationData":[OSD([sQuery(id+"F7.wireOp",EDGE,"E67")])]})]});}
            var Q5;
            Q5=makeQuery(id+"F8.boolean.opBoolean","INTERSECT",EDGE,{"disambiguationData":[OD(0.0)],"derivedFrom":[makeQuery(id+"F5.opExtrude","SWEPT_FACE",FACE,{"disambiguationData":[OSD([sQuery(id+"F4.wireOp",EDGE,"E30")])]}),makeQuery(id+"F8.opExtrude","SWEPT_FACE",FACE,{"disambiguationData":[OSD([sQuery(id+"F7.wireOp",EDGE,"E67")])]})]});
            fillet(context, id + "F14", {"entities" : qUnion([Q0, Q1, Q2, Q3, Q4, Q5]), "radius" : 3 * mm, "tangentPropagation" : true, "allowEdgeOverflow" : false});
        }
        {
            var Q0;
            Q0=makeQuery(id+"F1.opExtrude","CAP_EDGE",EDGE,{"disambiguationData":[OSD([sQuery(id+"F0.wireOp",EDGE,"E1.bottom")])],"isStart":false});
            fillet(context, id + "F15", {"entities" : qUnion([Q0]), "radius" : 2 * mm, "tangentPropagation" : true, "allowEdgeOverflow" : false});
        }
        {
            var Q0;
            {var subQ0=sQuery(id+"F0.wireOp",EDGE,"E21.filletArc");var subQ1=sQuery(id+"F0.wireOp",EDGE,"E7");var subQ2=sQuery(id+"F0.wireOp",EDGE,"E6");var subQ3=sQuery(id+"F0.wireOp",EDGE,"E5");var subQ4=sQuery(id+"F0.wireOp",EDGE,"E4");var subQ5=sQuery(id+"F0.wireOp",EDGE,"E22.filletArc");var subQ6=sQuery(id+"F0.wireOp",EDGE,"E1.bottom");var subQ7=sQuery(id+"F0.wireOp",EDGE,"E1.right");var subQ8=sQuery(id+"F0.wireOp",EDGE,"E1.top");var subQ9=sQuery(id+"F0.wireOp",EDGE,"E1.left");var subQ10=sQuery(id+"F0.wireOp",EDGE,"E23.filletArc");var subQ11=sQuery(id+"F0.wireOp",EDGE,"E24.filletArc");Q0=makeQuery(id+"F2.boolean.opBoolean","SPLIT",FACE,{"disambiguationData":[TD([makeQuery(id+"F1.opExtrude","SWEPT_FACE",FACE,{"disambiguationData":[OSD([subQ6])]})])],"derivedFrom":makeQuery(id+"F1.opExtrude","CAP_FACE",FACE,{"disambiguationData":[OSD([subQ6,subQ8,subQ9,subQ7,subQ4,subQ3,subQ2,subQ1,subQ0,subQ5,subQ10,subQ11])],"isStart":true})});}
            var sketch = newSketch(context, id + "F16", { "sketchPlane" : qUnion([Q0])});
            skLineSegment(sketch, "E79", {"start": v(-20.49, 104.25) * mm, "end": v(-20.49, 92.25) * mm});
            skLineSegment(sketch, "E80", {"start": v(-20.49, 92.25) * mm, "end": v(-38.49, 74.25) * mm});
            skLineSegment(sketch, "E81", {"start": v(9.51, 104.25) * mm, "end": v(9.51, 92.25) * mm});
            skLineSegment(sketch, "E82", {"start": v(9.51, 92.25) * mm, "end": v(27.51, 74.25) * mm});
            skArc(sketch, "E83", {"start": v(9.51, 104.25) * mm, "mid": v(-5.49, 119.25) * mm, "end": v(-20.49, 104.25) * mm});
            skCircle(sketch, "E84", {"center": v(-5.49, 104.25) * mm, "radius": 6 * mm});
            skLineSegment(sketch, "E85", {"start": v(-5.49, 104.25) * mm, "end": v(-5.49, 74.25) * mm, "construction": true});
            skLineSegment(sketch, "E86", {"start": v(-74.25, 0) * mm, "end": v(74.25, 0) * mm, "construction": true});
            skLineSegment(sketch, "E87.MirrorCS", {"start": v(-20.49, -92.25) * mm, "end": v(-38.49, -74.25) * mm});
            skLineSegment(sketch, "E88.MirrorCS", {"start": v(-20.49, -104.25) * mm, "end": v(-20.49, -92.25) * mm});
            skArc(sketch, "E89.MirrorCS", {"start": v(9.51, -104.25) * mm, "mid": v(-5.49, -119.25) * mm, "end": v(-20.49, -104.25) * mm});
            skCircle(sketch, "E90.MirrorC", {"center": v(-5.49, -104.25) * mm, "radius": 6 * mm});
            skLineSegment(sketch, "E91.MirrorCS", {"start": v(-5.49, -104.25) * mm, "end": v(-5.49, -74.25) * mm, "construction": true});
            skLineSegment(sketch, "E92.MirrorCS", {"start": v(9.51, -92.25) * mm, "end": v(27.51, -74.25) * mm});
            skLineSegment(sketch, "E93.MirrorCS", {"start": v(9.51, -104.25) * mm, "end": v(9.51, -92.25) * mm});
            skSolve(sketch);
        }
        {
            var Q0;
            Q0=makeQuery(id+"F16.imprint","IMPRINT",FACE,{"disambiguationData":[TD([[makeQuery(id+"F16.imprint","IMPRINT",EDGE,{"derivedFrom":sQuery(id+"F16.wireOp",EDGE,"E79")}),1.0]])]});
            var Q1;
            {var subQ0=sQuery(id+"F16.wireOp",EDGE,"E87.MirrorCS");Q1=makeQuery(id+"F16.imprint","IMPRINT",FACE,{"disambiguationData":[TD([[makeQuery(id+"F16.imprint","IMPRINT",EDGE,{"derivedFrom":subQ0}),-1.0]])]});}
            var Q2;
            Q2=makeQuery(id+"F2.opExtrude","CAP_FACE",FACE,{"disambiguationData":[OSD([sQuery(id+"F0.wireOp",EDGE,"E12"),sQuery(id+"F0.wireOp",EDGE,"E13"),sQuery(id+"F0.wireOp",EDGE,"E14"),sQuery(id+"F0.wireOp",EDGE,"E15"),sQuery(id+"F0.wireOp",EDGE,"E17.filletArc"),sQuery(id+"F0.wireOp",EDGE,"E18.filletArc"),sQuery(id+"F0.wireOp",EDGE,"E19.filletArc"),sQuery(id+"F0.wireOp",EDGE,"E20.filletArc"),sQuery(id+"F0.wireOp",EDGE,"E25.0"),sQuery(id+"F0.wireOp",EDGE,"E25.1"),sQuery(id+"F0.wireOp",EDGE,"E25.2"),sQuery(id+"F0.wireOp",EDGE,"E25.3"),sQuery(id+"F0.wireOp",EDGE,"E25.4"),sQuery(id+"F0.wireOp",EDGE,"E25.5"),sQuery(id+"F0.wireOp",EDGE,"E25.6"),sQuery(id+"F0.wireOp",EDGE,"E25.7")])],"isStart":false});
            extrude(context, id + "F17", {"entities" : qUnion([Q0, Q1]), "endBound" : BoundingType.UP_TO_SURFACE, "depth" : 25 * mm, "endBoundEntityFace" : qUnion([Q2]), "offsetDistance" : 25 * mm});
        }
    });
